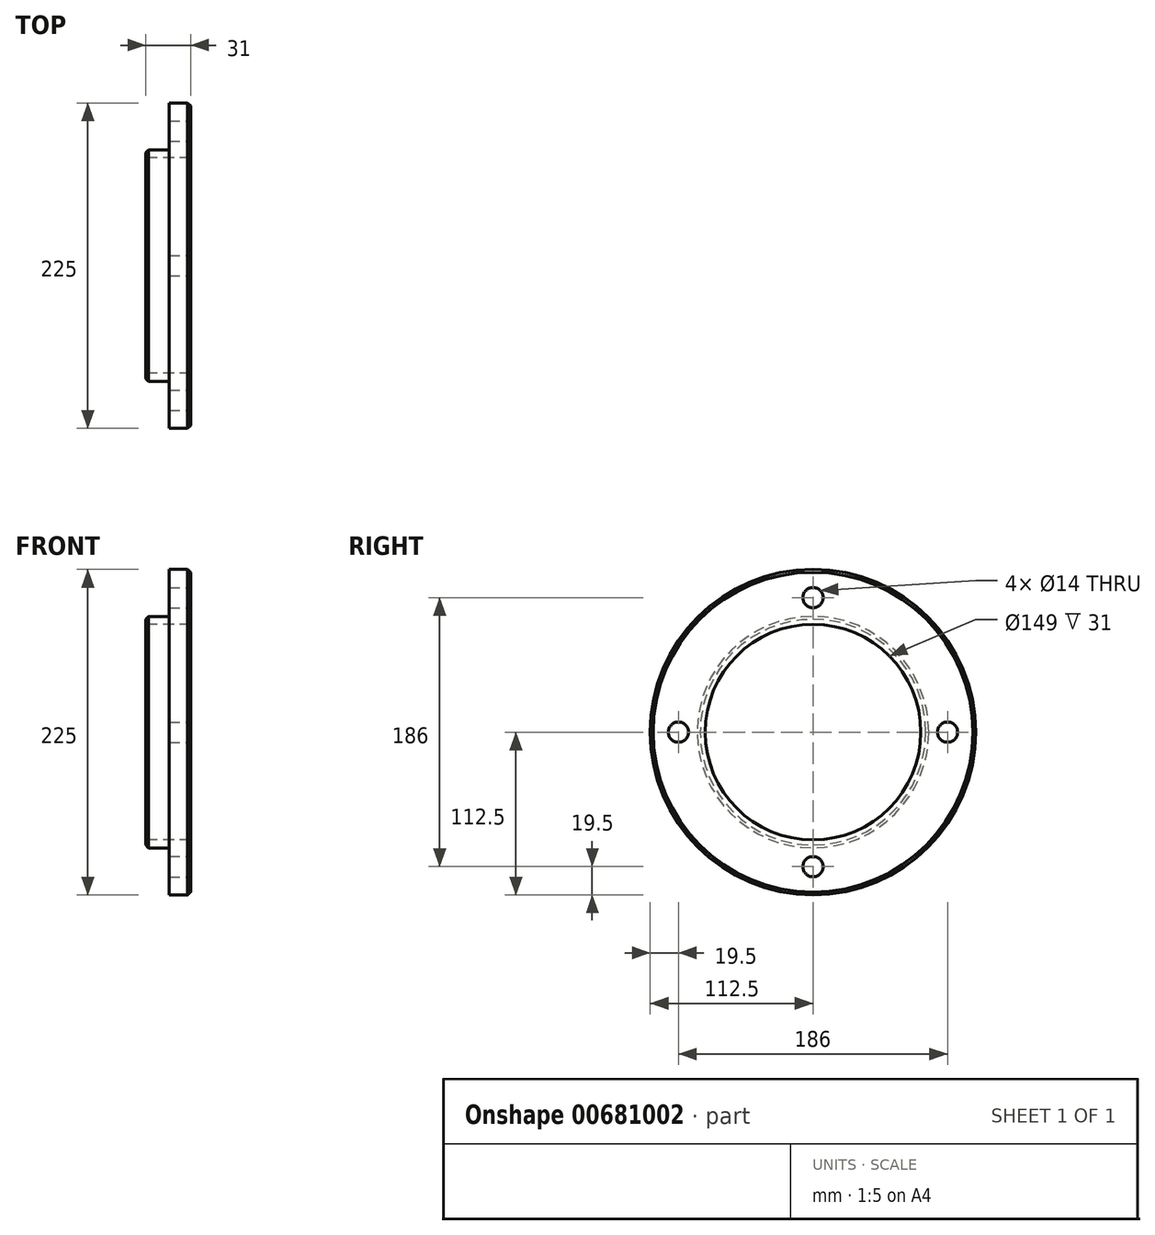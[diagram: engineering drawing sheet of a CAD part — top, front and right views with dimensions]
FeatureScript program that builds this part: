
annotation { "Feature Type Name" : "Feature", "Feature Type Description" : "" }
export const myFeature = defineFeature(function(context is Context, id is Id, definition is map)
    precondition{}
    {
        {
            var Q0;
            Q0=qCreatedBy(makeId("Right.planeOp"),FACE);
            var sketch = newSketch(context, id + "F0", { "sketchPlane" : qUnion([Q0])});
            skCircle(sketch, "E0", {"center": v(0, 0) * mm, "radius": 112.5 * mm});
            skSolve(sketch);
        }
        {
            var Q0;
            Q0=qSketchRegion(id+"F0",true);
            extrude(context, id + "F1", {"entities" : qUnion([Q0]), "depth" : 14.9 * mm, "offsetDistance" : 25 * mm});
        }
        {
            var Q0;
            Q0=makeQuery(id+"F1.opExtrude","CAP_FACE",FACE,{"disambiguationData":[OSD([sQuery(id+"F0.wireOp",EDGE,"E0")])],"isStart":true});
            var sketch = newSketch(context, id + "F2", { "sketchPlane" : qUnion([Q0])});
            skCircle(sketch, "E1", {"center": v(0, 0) * mm, "radius": 80 * mm});
            skSolve(sketch);
        }
        {
            var Q0;
            Q0=qSketchRegion(id+"F2",true);
            extrude(context, id + "F3", {"entities" : qUnion([Q0]), "operationType" : NewBodyOperationType.ADD, "depth" : 16.1 * mm, "offsetDistance" : 25 * mm});
        }
        {
            var Q0;
            Q0=makeQuery(id+"F3.opExtrude","CAP_EDGE",EDGE,{"disambiguationData":[OSD([sQuery(id+"F2.wireOp",EDGE,"E1")])],"isStart":false});
            var Q1;
            Q1=makeQuery(id+"F1.opExtrude","CAP_EDGE",EDGE,{"disambiguationData":[OSD([sQuery(id+"F0.wireOp",EDGE,"E0")])],"isStart":false});
            chamfer(context, id + "F4", {"entities" : qUnion([Q0, Q1]), "width" : 2 * mm, "tangentPropagation" : true});
        }
        {
            var Q0;
            Q0=makeQuery(id+"F3.opExtrude","CAP_FACE",FACE,{"disambiguationData":[OSD([sQuery(id+"F2.wireOp",EDGE,"E1")])],"isStart":false});
            var sketch = newSketch(context, id + "F5", { "sketchPlane" : qUnion([Q0])});
            skCircle(sketch, "E2", {"center": v(0, 0) * mm, "radius": 74.5 * mm});
            skSolve(sketch);
        }
        {
            var Q0;
            Q0=qSketchRegion(id+"F5",true);
            extrude(context, id + "F6", {"entities" : qUnion([Q0]), "operationType" : NewBodyOperationType.REMOVE, "endBound" : BoundingType.THROUGH_ALL, "oppositeDirection" : true, "depth" : 25 * mm, "offsetDistance" : 25 * mm});
        }
        {
            var Q0;
            Q0=makeQuery(id+"F1.opExtrude","CAP_FACE",FACE,{"disambiguationData":[OSD([sQuery(id+"F0.wireOp",EDGE,"E0")])],"isStart":false});
            var sketch = newSketch(context, id + "F7", { "sketchPlane" : qUnion([Q0])});
            skCircle(sketch, "E3", {"center": v(0, 0) * mm, "radius": 93 * mm, "construction": true});
            skLineSegment(sketch, "E4", {"start": v(0, 0) * mm, "end": v(0, -93) * mm, "construction": true});
            skPoint(sketch, "E5", {"position": v(0, -93) * mm});
            skPoint(sketch, "E6.1.0", {"position": v(93, 0) * mm});
            skPoint(sketch, "E6.2.0", {"position": v(0, 93) * mm});
            skPoint(sketch, "E6.3.0", {"position": v(-93, 0) * mm});
            skSolve(sketch);
        }
        {
            var Q0;
            Q0=sQuery(id+"F7.wireOp",VERTEX,"E5");
            var Q1;
            Q1=sQuery(id+"F7.wireOp",VERTEX,"E6.3.0");
            var Q2;
            Q2=sQuery(id+"F7.wireOp",VERTEX,"E6.2.0");
            var Q3;
            Q3=sQuery(id+"F7.wireOp",VERTEX,"E6.1.0");
            var Q4;
            Q4=makeQuery(id+"F1.opExtrude","SWEPT_BODY",BODY,{"disambiguationData":[OSD([sQuery(id+"F0.wireOp",EDGE,"E0")])]});
            hole(context, id + "F8", {"style" : HoleStyle.SIMPLE, "endStyle" : HoleEndStyle.THROUGH, "holeDiameter" : 14 * mm, "majorDiameter" : 5 * mm, "isTappedThrough" : true, "tappedDepth" : 24.75 * mm, "tapClearance" : 3, "locations" : qUnion([Q0, Q1, Q2, Q3]), "scope" : qUnion([Q4])});
        }
    });
